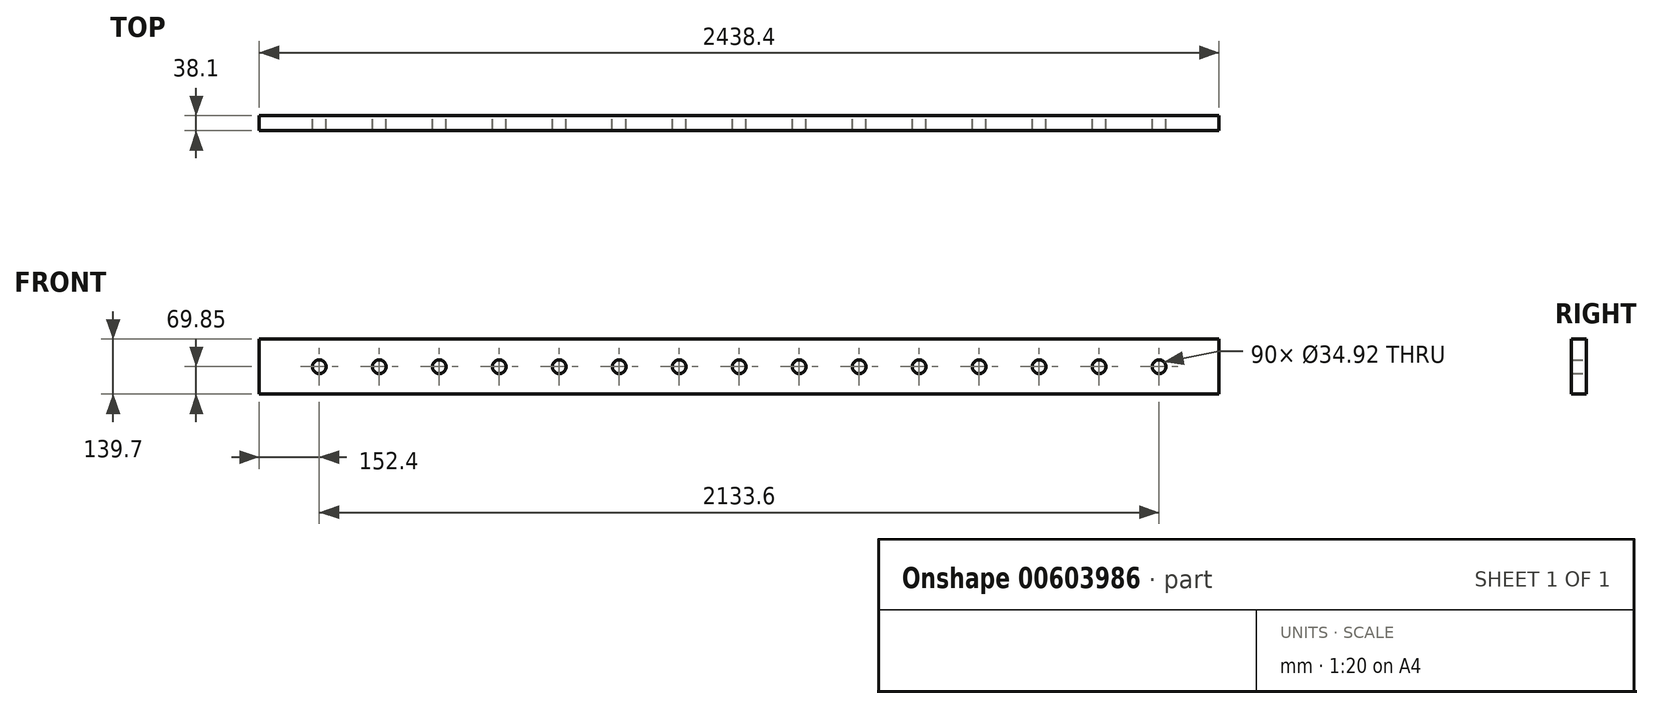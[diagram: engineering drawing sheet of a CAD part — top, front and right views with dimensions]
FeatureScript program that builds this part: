
annotation { "Feature Type Name" : "Feature", "Feature Type Description" : "" }
export const myFeature = defineFeature(function(context is Context, id is Id, definition is map)
    precondition{}
    {
        {
            var Q0;
            Q0=qCreatedBy(makeId("Front.planeOp"),FACE);
            var sketch = newSketch(context, id + "F0", { "sketchPlane" : qUnion([Q0])});
            skLineSegment(sketch, "E0.bottom", {"start": v(0, 0) * mm, "end": v(2438.4, 0) * mm});
            skLineSegment(sketch, "E0.top", {"start": v(0, 139.7) * mm, "end": v(2438.4, 139.7) * mm});
            skLineSegment(sketch, "E0.left", {"start": v(0, 0) * mm, "end": v(0, 139.7) * mm});
            skLineSegment(sketch, "E0.right", {"start": v(2438.4, 0) * mm, "end": v(2438.4, 139.7) * mm});
            skLineSegment(sketch, "E1", {"start": v(0, 69.85) * mm, "end": v(2561.75, 69.85) * mm, "construction": true});
            skCircle(sketch, "E2", {"center": v(152.4, 69.85) * mm, "radius": 17.46 * mm});
            skCircle(sketch, "E3.1.0.0", {"center": v(304.8, 69.85) * mm, "radius": 17.46 * mm});
            skCircle(sketch, "E3.2.0.0", {"center": v(457.2, 69.85) * mm, "radius": 17.46 * mm});
            skCircle(sketch, "E3.3.0.0", {"center": v(609.6, 69.85) * mm, "radius": 17.46 * mm});
            skCircle(sketch, "E3.4.0.0", {"center": v(762, 69.85) * mm, "radius": 17.46 * mm});
            skCircle(sketch, "E3.5.0.0", {"center": v(914.4, 69.85) * mm, "radius": 17.46 * mm});
            skCircle(sketch, "E3.6.0.0", {"center": v(1066.8, 69.85) * mm, "radius": 17.46 * mm});
            skCircle(sketch, "E3.7.0.0", {"center": v(1219.2, 69.85) * mm, "radius": 17.46 * mm});
            skCircle(sketch, "E3.8.0.0", {"center": v(1371.6, 69.85) * mm, "radius": 17.46 * mm});
            skCircle(sketch, "E3.9.0.0", {"center": v(1524, 69.85) * mm, "radius": 17.46 * mm});
            skCircle(sketch, "E3.10.0.0", {"center": v(1676.4, 69.85) * mm, "radius": 17.46 * mm});
            skCircle(sketch, "E3.11.0.0", {"center": v(1828.8, 69.85) * mm, "radius": 17.46 * mm});
            skCircle(sketch, "E3.12.0.0", {"center": v(1981.2, 69.85) * mm, "radius": 17.46 * mm});
            skCircle(sketch, "E3.13.0.0", {"center": v(2133.6, 69.85) * mm, "radius": 17.46 * mm});
            skCircle(sketch, "E3.14.0.0", {"center": v(2286, 69.85) * mm, "radius": 17.46 * mm});
            skLineSegment(sketch, "E3.direction1", {"start": v(152.4, 69.85) * mm, "end": v(304.8, 69.85) * mm, "construction": true});
            skSolve(sketch);
        }
        {
            var Q0;
            Q0=makeQuery(id+"F0.imprint","IMPRINT",FACE,{"disambiguationData":[TD([[makeQuery(id+"F0.imprint","IMPRINT",EDGE,{"derivedFrom":sQuery(id+"F0.wireOp",EDGE,"E0.bottom")}),1.0]])]});
            extrude(context, id + "F1", {"entities" : qUnion([Q0]), "depth" : 38.1 * mm, "offsetDistance" : 25.4 * mm});
        }
    });
